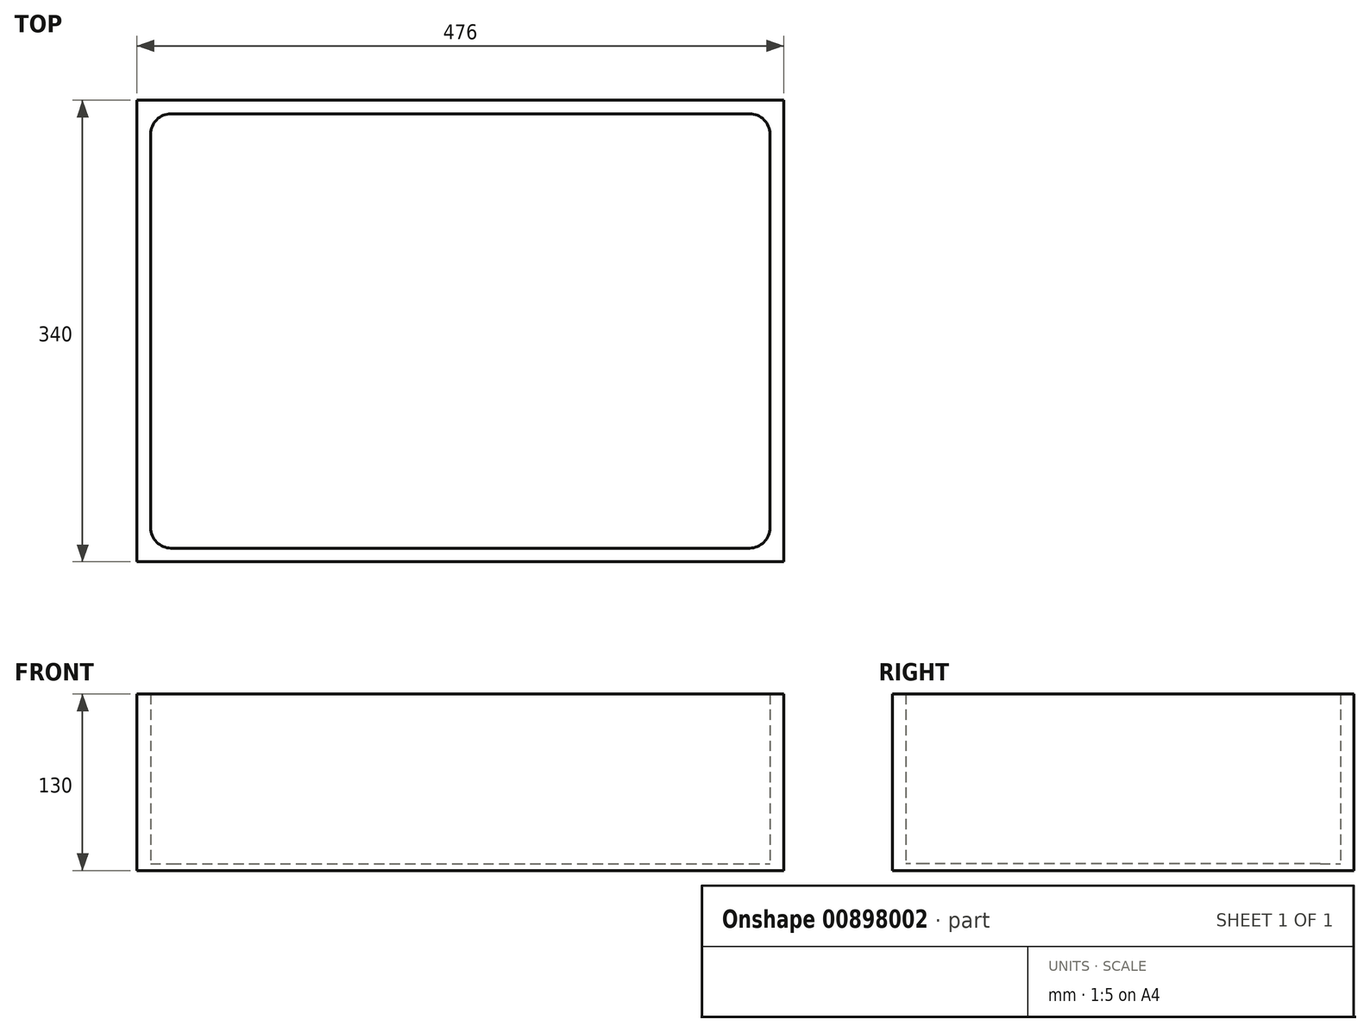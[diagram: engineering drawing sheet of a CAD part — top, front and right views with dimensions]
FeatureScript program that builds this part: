
annotation { "Feature Type Name" : "Feature", "Feature Type Description" : "" }
export const myFeature = defineFeature(function(context is Context, id is Id, definition is map)
    precondition{}
    {
        {
            var Q0;
            Q0=qCreatedBy(makeId("Top.planeOp"),FACE);
            var sketch = newSketch(context, id + "F0", { "sketchPlane" : qUnion([Q0])});
            skLineSegment(sketch, "E0.bottom", {"start": v(-380.27, 292.37) * mm, "end": v(75.73, 292.37) * mm});
            skLineSegment(sketch, "E0.top", {"start": v(-380.27, -27.63) * mm, "end": v(75.73, -27.63) * mm});
            skLineSegment(sketch, "E0.left", {"start": v(-380.27, 292.37) * mm, "end": v(-380.27, -27.63) * mm});
            skLineSegment(sketch, "E0.right", {"start": v(75.73, 292.37) * mm, "end": v(75.73, -27.63) * mm});
            skLineSegment(sketch, "E1.0", {"start": v(-390.27, 302.37) * mm, "end": v(85.73, 302.37) * mm});
            skLineSegment(sketch, "E1.1", {"start": v(-390.27, 302.37) * mm, "end": v(-390.27, -37.63) * mm});
            skLineSegment(sketch, "E1.2", {"start": v(-390.27, -37.63) * mm, "end": v(85.73, -37.63) * mm});
            skLineSegment(sketch, "E1.3", {"start": v(85.73, 302.37) * mm, "end": v(85.73, -37.63) * mm});
            skSolve(sketch);
        }
        {
            var Q0;
            Q0=makeQuery(id+"F0.imprint","IMPRINT",FACE,{"disambiguationData":[TD([[makeQuery(id+"F0.imprint","IMPRINT",EDGE,{"derivedFrom":sQuery(id+"F0.wireOp",EDGE,"E0.bottom")}),1.0]])]});
            extrude(context, id + "F1", {"entities" : qUnion([Q0]), "depth" : 125 * mm, "offsetDistance" : 25 * mm});
        }
        {
            var Q0;
            Q0=makeQuery(id+"F0.imprint","IMPRINT",FACE,{"disambiguationData":[TD([[makeQuery(id+"F0.imprint","IMPRINT",EDGE,{"derivedFrom":sQuery(id+"F0.wireOp",EDGE,"E0.bottom")}),-1.0]])]});
            var Q1;
            Q1=makeQuery(id+"F0.imprint","IMPRINT",FACE,{"disambiguationData":[TD([[makeQuery(id+"F0.imprint","IMPRINT",EDGE,{"derivedFrom":sQuery(id+"F0.wireOp",EDGE,"E0.bottom")}),1.0]])]});
            extrude(context, id + "F2", {"entities" : qUnion([Q0, Q1]), "operationType" : NewBodyOperationType.ADD, "oppositeDirection" : true, "depth" : 5 * mm, "offsetDistance" : 25 * mm});
        }
        {
            var Q0;
            Q0=makeQuery(id+"F1.opExtrude","SWEPT_EDGE",EDGE,{"disambiguationData":[OSD([sQuery(id+"F0.wireOp",EDGE,"E0.bottom"),sQuery(id+"F0.wireOp",EDGE,"E0.right")])]});
            var Q1;
            Q1=makeQuery(id+"F1.opExtrude","SWEPT_EDGE",EDGE,{"disambiguationData":[OSD([sQuery(id+"F0.wireOp",EDGE,"E0.bottom"),sQuery(id+"F0.wireOp",EDGE,"E0.left")])]});
            var Q2;
            Q2=makeQuery(id+"F1.opExtrude","SWEPT_EDGE",EDGE,{"disambiguationData":[OSD([sQuery(id+"F0.wireOp",EDGE,"E0.top"),sQuery(id+"F0.wireOp",EDGE,"E0.right")])]});
            var Q3;
            Q3=makeQuery(id+"F1.opExtrude","SWEPT_EDGE",EDGE,{"disambiguationData":[OSD([sQuery(id+"F0.wireOp",EDGE,"E0.top"),sQuery(id+"F0.wireOp",EDGE,"E0.left")])]});
            var Q4;
            Q4=makeQuery(id+"F1.opExtrude","CAP_EDGE",EDGE,{"disambiguationData":[OSD([sQuery(id+"F0.wireOp",EDGE,"E0.top")])],"isStart":true});
            var Q5;
            Q5=makeQuery(id+"F1.opExtrude","CAP_EDGE",EDGE,{"disambiguationData":[OSD([sQuery(id+"F0.wireOp",EDGE,"E0.left")])],"isStart":true});
            var Q6;
            Q6=makeQuery(id+"F1.opExtrude","CAP_EDGE",EDGE,{"disambiguationData":[OSD([sQuery(id+"F0.wireOp",EDGE,"E0.bottom")])],"isStart":true});
            var Q7;
            Q7=makeQuery(id+"F1.opExtrude","CAP_EDGE",EDGE,{"disambiguationData":[OSD([sQuery(id+"F0.wireOp",EDGE,"E0.right")])],"isStart":true});
            fillet(context, id + "F3", {"entities" : qUnion([Q0, Q1, Q2, Q3, Q4, Q5, Q6, Q7]), "radius" : 15 * mm, "tangentPropagation" : true, "allowEdgeOverflow" : false});
        }
    });
